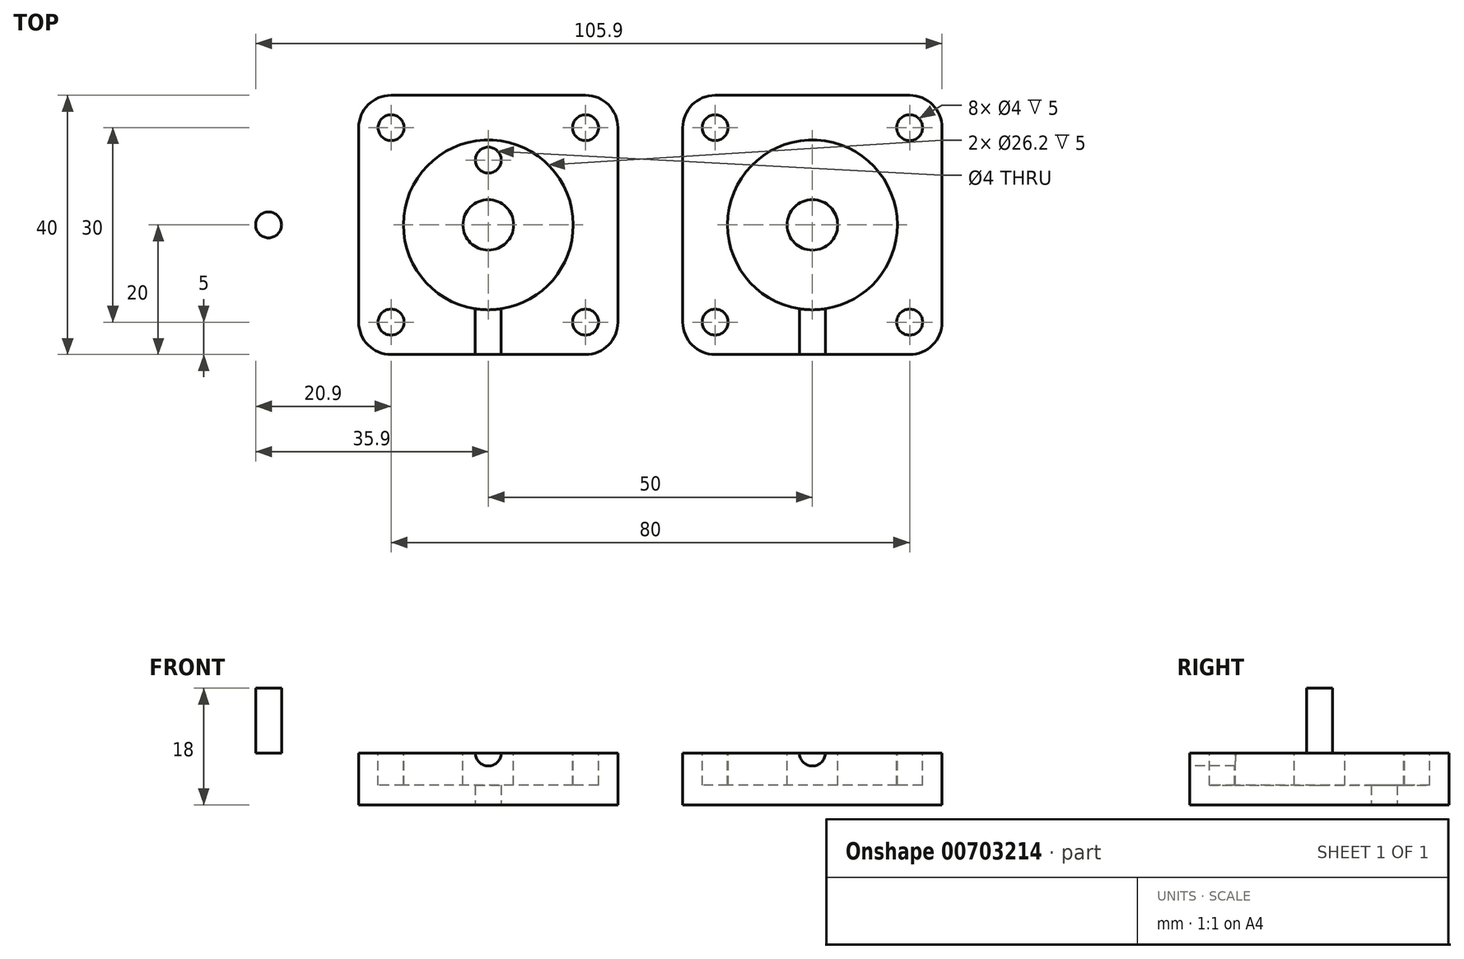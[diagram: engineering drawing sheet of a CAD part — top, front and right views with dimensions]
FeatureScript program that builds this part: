
annotation { "Feature Type Name" : "Feature", "Feature Type Description" : "" }
export const myFeature = defineFeature(function(context is Context, id is Id, definition is map)
    precondition{}
    {
        {
            var Q0;
            Q0=qCreatedBy(makeId("Top.planeOp"),FACE);
            var sketch = newSketch(context, id + "F0", { "sketchPlane" : qUnion([Q0])});
            skLineSegment(sketch, "E0.bottom", {"start": v(-15, 20) * mm, "end": v(15, 20) * mm});
            skLineSegment(sketch, "E0.top", {"start": v(-15, -20) * mm, "end": v(15, -20) * mm});
            skLineSegment(sketch, "E0.left", {"start": v(-20, 15) * mm, "end": v(-20, -15) * mm});
            skLineSegment(sketch, "E0.right", {"start": v(20, 15) * mm, "end": v(20, -15) * mm});
            skPoint(sketch, "E1.visualSharp", {"position": v(-20, -20) * mm});
            skArc(sketch, "E1.filletArc", {"start": v(-20, -15) * mm, "mid": v(-18.54, -18.54) * mm, "end": v(-15, -20) * mm});
            skPoint(sketch, "E2.visualSharp", {"position": v(20, -20) * mm});
            skArc(sketch, "E2.filletArc", {"start": v(15, -20) * mm, "mid": v(18.54, -18.54) * mm, "end": v(20, -15) * mm});
            skPoint(sketch, "E3.visualSharp", {"position": v(20, 20) * mm});
            skArc(sketch, "E3.filletArc", {"start": v(20, 15) * mm, "mid": v(18.54, 18.54) * mm, "end": v(15, 20) * mm});
            skPoint(sketch, "E4.visualSharp", {"position": v(-20, 20) * mm});
            skArc(sketch, "E4.filletArc", {"start": v(-15, 20) * mm, "mid": v(-18.54, 18.54) * mm, "end": v(-20, 15) * mm});
            skSolve(sketch);
        }
        {
            var Q0;
            Q0 = qSketchRegion(id + "F0", true);
            extrude(context, id + "F1", {"entities" : qUnion([Q0]), "oppositeDirection" : true, "depth" : 8 * mm, "offsetDistance" : 25 * mm});
        }
        {
            var Q0;
            Q0=makeQuery(id+"F1.opExtrude","CAP_FACE",FACE,{"disambiguationData":[OSD([sQuery(id+"F0.wireOp",EDGE,"E0.bottom"),sQuery(id+"F0.wireOp",EDGE,"E0.top"),sQuery(id+"F0.wireOp",EDGE,"E0.left"),sQuery(id+"F0.wireOp",EDGE,"E0.right"),sQuery(id+"F0.wireOp",EDGE,"E1.filletArc"),sQuery(id+"F0.wireOp",EDGE,"E2.filletArc"),sQuery(id+"F0.wireOp",EDGE,"E3.filletArc"),sQuery(id+"F0.wireOp",EDGE,"E4.filletArc")])],"isStart":true});
            var sketch = newSketch(context, id + "F2", { "sketchPlane" : qUnion([Q0])});
            skCircle(sketch, "E5", {"center": v(0, 0) * mm, "radius": 13.1 * mm});
            skCircle(sketch, "E6", {"center": v(0, 0) * mm, "radius": 3.9 * mm});
            skCircle(sketch, "E7", {"center": v(-15, -15) * mm, "radius": 2 * mm});
            skCircle(sketch, "E8", {"center": v(-15, 15) * mm, "radius": 2 * mm});
            skCircle(sketch, "E9", {"center": v(15, 15) * mm, "radius": 2 * mm});
            skCircle(sketch, "E10", {"center": v(15, -15) * mm, "radius": 2 * mm});
            skSolve(sketch);
        }
        {
            var Q0;
            Q0 = qSketchRegion(id + "F2", true);
            extrude(context, id + "F3", {"entities" : qUnion([Q0]), "operationType" : NewBodyOperationType.REMOVE, "oppositeDirection" : true, "depth" : 5 * mm, "offsetDistance" : 25 * mm});
        }
        {
            var Q0;
            Q0=makeQuery(id+"F1.opExtrude","SWEPT_FACE",FACE,{"disambiguationData":[OSD([sQuery(id+"F0.wireOp",EDGE,"E0.top")])]});
            var sketch = newSketch(context, id + "F4", { "sketchPlane" : qUnion([Q0])});
            skCircle(sketch, "E11", {"center": v(0, 0) * mm, "radius": 2 * mm});
            skSolve(sketch);
        }
        {
            var Q0;
            Q0 = qSketchRegion(id + "F4", true);
            extrude(context, id + "F5", {"entities" : qUnion([Q0]), "operationType" : NewBodyOperationType.REMOVE, "oppositeDirection" : true, "depth" : 10 * mm, "offsetDistance" : 25 * mm});
        }
        {
            var Q0;
            Q0=makeQuery(id+"F1.opExtrude","SWEPT_BODY",BODY,{"disambiguationData":[OSD([sQuery(id+"F0.wireOp",EDGE,"E0.bottom"),sQuery(id+"F0.wireOp",EDGE,"E0.top"),sQuery(id+"F0.wireOp",EDGE,"E0.left"),sQuery(id+"F0.wireOp",EDGE,"E0.right"),sQuery(id+"F0.wireOp",EDGE,"E1.filletArc"),sQuery(id+"F0.wireOp",EDGE,"E2.filletArc"),sQuery(id+"F0.wireOp",EDGE,"E3.filletArc"),sQuery(id+"F0.wireOp",EDGE,"E4.filletArc")])]});
            transform(context, id + "F6", {"entities" : qUnion([Q0]), "transformType" : TransformType.TRANSLATION_3D, "dx" : 50 * mm, "dy" : 0 * mm, "dz" : 0 * mm, "makeCopy" : true});
        }
        {
            var Q0;
            Q0=makeQuery(id+"F1.opExtrude","CAP_FACE",FACE,{"disambiguationData":[OSD([sQuery(id+"F0.wireOp",EDGE,"E0.bottom"),sQuery(id+"F0.wireOp",EDGE,"E0.top"),sQuery(id+"F0.wireOp",EDGE,"E0.left"),sQuery(id+"F0.wireOp",EDGE,"E0.right"),sQuery(id+"F0.wireOp",EDGE,"E1.filletArc"),sQuery(id+"F0.wireOp",EDGE,"E2.filletArc"),sQuery(id+"F0.wireOp",EDGE,"E3.filletArc"),sQuery(id+"F0.wireOp",EDGE,"E4.filletArc")])],"isStart":false});
            var sketch = newSketch(context, id + "F7", { "sketchPlane" : qUnion([Q0])});
            skCircle(sketch, "E12", {"center": v(0, -10) * mm, "radius": 2 * mm});
            skSolve(sketch);
        }
        {
            var Q0;
            Q0 = qSketchRegion(id + "F7", true);
            extrude(context, id + "F8", {"entities" : qUnion([Q0]), "operationType" : NewBodyOperationType.REMOVE, "oppositeDirection" : true, "depth" : 3 * mm, "offsetDistance" : 25 * mm});
        }
        {
            var Q0;
            Q0=qCreatedBy(makeId("Top.planeOp"),FACE);
            var sketch = newSketch(context, id + "F9", { "sketchPlane" : qUnion([Q0])});
            skCircle(sketch, "E13", {"center": v(-33.9, 0) * mm, "radius": 2 * mm});
            skSolve(sketch);
        }
        {
            var Q0;
            Q0 = qSketchRegion(id + "F9", true);
            extrude(context, id + "F10", {"entities" : qUnion([Q0]), "depth" : 10 * mm, "offsetDistance" : 25 * mm});
        }
    });
